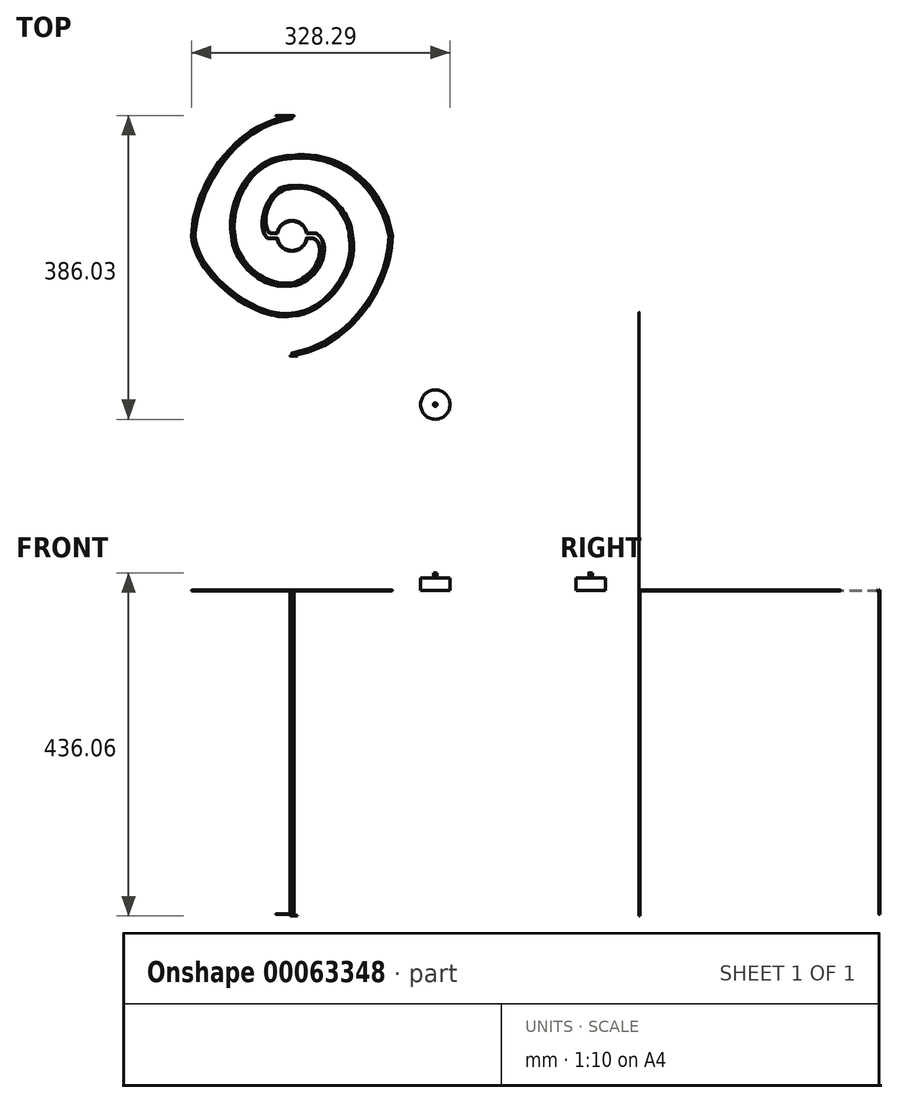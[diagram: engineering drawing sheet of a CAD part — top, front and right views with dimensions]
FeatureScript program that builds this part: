
annotation { "Feature Type Name" : "Feature", "Feature Type Description" : "" }
export const myFeature = defineFeature(function(context is Context, id is Id, definition is map)
    precondition{}
    {
        {
            var Q0;
            Q0=qCreatedBy(makeId("Top.planeOp"),FACE);
            var sketch = newSketch(context, id + "F0", { "sketchPlane" : qUnion([Q0])});
            skArc(sketch, "E0", {"start": v(0, 89.77) * mm, "mid": v(-59.8, 59.94) * mm, "end": v(-89.32, 0) * mm});
            skArc(sketch, "E1", {"start": v(-89.32, 0) * mm, "mid": v(-62.36, -58.9) * mm, "end": v(0, -76.43) * mm});
            skArc(sketch, "E2", {"start": v(0, -76.43) * mm, "mid": v(50.12, -52.11) * mm, "end": v(69.78, 0) * mm});
            skArc(sketch, "E3", {"start": v(69.78, 0) * mm, "mid": v(43.04, 36.2) * mm, "end": v(0, 49.33) * mm});
            skArc(sketch, "E4", {"start": v(0, 49.33) * mm, "mid": v(-33.38, 33.39) * mm, "end": v(-49.32, 0) * mm});
            skArc(sketch, "E5", {"start": v(-49.32, 0) * mm, "mid": v(-33.62, -32.42) * mm, "end": v(0, -45.36) * mm});
            skArc(sketch, "E6", {"start": v(0, -45.36) * mm, "mid": v(28.3, -30.82) * mm, "end": v(36.16, 0) * mm});
            skArc(sketch, "E7", {"start": v(36.16, 0) * mm, "mid": v(22.2, 17.77) * mm, "end": v(0, 22) * mm});
            skArc(sketch, "E8", {"start": v(0, 22) * mm, "mid": v(-15.87, 15.65) * mm, "end": v(-22.73, 0) * mm});
            skArc(sketch, "E9", {"start": v(-22.73, 0) * mm, "mid": v(-20.93, -10.33) * mm, "end": v(-11.38, -14.66) * mm});
            skLineSegment(sketch, "E10", {"start": v(-11.38, -14.66) * mm, "end": v(-4.56, -14.24) * mm});
            skArc(sketch, "E11", {"start": v(-4.56, -14.24) * mm, "mid": v(3.25, -18.93) * mm, "end": v(11.06, -14.24) * mm});
            skLineSegment(sketch, "E12", {"start": v(11.06, -14.24) * mm, "end": v(18.26, -14.24) * mm});
            skArc(sketch, "E13", {"start": v(0, -26.3) * mm, "mid": v(11.6, -24.01) * mm, "end": v(18.26, -14.24) * mm});
            skArc(sketch, "E14", {"start": v(-31.78, 0) * mm, "mid": v(-21.36, -19.76) * mm, "end": v(0, -26.3) * mm});
            skArc(sketch, "E15", {"start": v(0, 31.04) * mm, "mid": v(-22.27, 22.05) * mm, "end": v(-31.78, 0) * mm});
            skArc(sketch, "E16", {"start": v(45.44, 0) * mm, "mid": v(28.67, 24.24) * mm, "end": v(0, 31.04) * mm});
            skArc(sketch, "E17", {"start": v(0, -54.54) * mm, "mid": v(34.81, -37.34) * mm, "end": v(45.44, 0) * mm});
            skArc(sketch, "E18", {"start": v(-68.7, 0) * mm, "mid": v(-45.81, -41.72) * mm, "end": v(0, -54.54) * mm});
            skArc(sketch, "E19", {"start": v(0, 58.55) * mm, "mid": v(-46.84, 43.93) * mm, "end": v(-68.7, 0) * mm});
            skArc(sketch, "E20", {"start": v(83.03, 0) * mm, "mid": v(51.48, 43.4) * mm, "end": v(0, 58.55) * mm});
            skArc(sketch, "E21", {"start": v(0, -90.65) * mm, "mid": v(60.43, -62.65) * mm, "end": v(83.03, 0) * mm});
            skSolve(sketch);
        }
        {
            var Q0;
            Q0=qCreatedBy(makeId("Top.planeOp"),FACE);
            var sketch = newSketch(context, id + "F1", { "sketchPlane" : qUnion([Q0])});
            skCircle(sketch, "E22", {"center": v(353.44, -9.02) * mm, "radius": 19.05 * mm});
            skCircle(sketch, "E23", {"center": v(353.44, -9.02) * mm, "radius": 38.5 * mm});
            skCircle(sketch, "E24", {"center": v(353.44, -9.02) * mm, "radius": 41.67 * mm});
            skCircle(sketch, "E25", {"center": v(353.44, -9.02) * mm, "radius": 84.25 * mm});
            skCircle(sketch, "E26", {"center": v(353.44, -9.02) * mm, "radius": 87.43 * mm});
            skCircle(sketch, "E27", {"center": v(353.44, -9.02) * mm, "radius": 149.22 * mm});
            skCircle(sketch, "E28", {"center": v(353.44, -9.02) * mm, "radius": 152.4 * mm});
            skLineSegment(sketch, "E29", {"start": v(353.44, -9.02) * mm, "end": v(148.9, -9.02) * mm, "construction": true});
            skLineSegment(sketch, "E30", {"start": v(148.9, -9.02) * mm, "end": v(530.73, -9.02) * mm, "construction": true});
            skPoint(sketch, "E30.endSnap0", {"position": v(251.17, -9.02) * mm});
            skFitSpline(sketch, "E31", {"points": [v(353.44, 143.38) * mm, v(223.56, -9.02) * mm, v(353.44, -96.44) * mm], "startDerivative": vector(-431.97, -40.6) * mm, "endDerivative": vector(377.83, 174.24) * mm});
            skFitSpline(sketch, "E32", {"points": [v(353.44, -96.44) * mm, v(412.8, -9.02) * mm], "startDerivative": vector(88.92, 25.68) * mm, "endDerivative": vector(-23.7, 167.58) * mm});
            skFitSpline(sketch, "E33", {"points": [v(412.8, -9.02) * mm, v(353.44, 32.65) * mm], "startDerivative": vector(-4.13, 75.4) * mm, "endDerivative": vector(-93.38, -20.84) * mm});
            skFitSpline(sketch, "E34", {"points": [v(353.44, 32.65) * mm, v(319.45, -9.02) * mm], "startDerivative": vector(-79.71, -28.71) * mm, "endDerivative": vector(3.4, -46.05) * mm});
            skLineSegment(sketch, "E35", {"start": v(319.45, -9.02) * mm, "end": v(319.45, -13.48) * mm});
            skLineSegment(sketch, "E36", {"start": v(319.45, -13.48) * mm, "end": v(334.92, -13.48) * mm});
            skArc(sketch, "E37", {"start": v(334.92, -13.48) * mm, "mid": v(353.44, -28.18) * mm, "end": v(371.95, -13.48) * mm});
            skLineSegment(sketch, "E38", {"start": v(371.95, -13.48) * mm, "end": v(380.93, -13.48) * mm});
            skFitSpline(sketch, "E39", {"points": [v(380.93, -13.48) * mm, v(353.44, -47.5) * mm], "startDerivative": vector(2.43, -44.73) * mm, "endDerivative": vector(-36.66, -5.97) * mm});
            skFitSpline(sketch, "E40", {"points": [v(353.44, -47.5) * mm, v(291.41, -9.02) * mm], "startDerivative": vector(-111.15, -35.33) * mm, "endDerivative": vector(9.25, 49.7) * mm});
            skFitSpline(sketch, "E41", {"points": [v(291.41, -9.02) * mm, v(353.09, 75.24) * mm], "startDerivative": vector(8.63, 128.1) * mm, "endDerivative": vector(83.56, 34.12) * mm});
            skFitSpline(sketch, "E42", {"points": [v(353.09, 75.24) * mm, v(470.5, -9.02) * mm], "startDerivative": vector(188.1, 69.59) * mm, "endDerivative": vector(-1.84, -118.92) * mm});
            skFitSpline(sketch, "E43", {"points": [v(470.5, -9.02) * mm, v(353.44, -158.24) * mm], "startDerivative": vector(5.2, -214.31) * mm, "endDerivative": vector(-145.21, 3.55) * mm});
            skLineSegment(sketch, "E44", {"start": v(353.44, -9.02) * mm, "end": v(353.44, 175.95) * mm, "construction": true});
            skLineSegment(sketch, "E45", {"start": v(353.44, 175.95) * mm, "end": v(353.44, -184.71) * mm, "construction": true});
            skSolve(sketch);
        }
        {
            var Q0;
            {var subQ0=sQuery(id+"F1.wireOp",EDGE,"E31");var subQ3=sQuery(id+"F1.wireOp",EDGE,"E27");var subQ4=makeQuery(id+"F1.imprint","INTERSECT",VERTEX,{"derivedFrom":[subQ3,subQ0]});Q0=makeQuery(id+"F1.imprint","IMPRINT",FACE,{"disambiguationData":[TD([[makeQuery(id+"F1.imprint","IMPRINT",EDGE,{"disambiguationData":[TD([[subQ4,1.0]])],"derivedFrom":subQ3}),1.0]])]});}
            var sketch = newSketch(context, id + "F2", { "sketchPlane" : qUnion([Q0])});
            skLineSegment(sketch, "E46", {"start": v(223.56, -9.02) * mm, "end": v(226.73, -9.02) * mm, "construction": true});
            skFitSpline(sketch, "E47", {"points": [v(353.44, 140.05) * mm, v(226.73, -9.02) * mm], "startDerivative": vector(-240.84, -35.76) * mm, "endDerivative": vector(17.36, -172.87) * mm});
            skFitSpline(sketch, "E48", {"points": [v(226.73, -9.02) * mm, v(353.45, -93.24) * mm], "startDerivative": vector(25.64, -131.53) * mm, "endDerivative": vector(239.43, 63.9) * mm});
            skLineSegment(sketch, "E49", {"start": v(412.8, -9.02) * mm, "end": v(409.62, -9.02) * mm, "construction": true});
            skFitSpline(sketch, "E50", {"points": [v(353.45, -93.24) * mm, v(409.62, -9.02) * mm], "startDerivative": vector(110.05, 33.72) * mm, "endDerivative": vector(-18.44, 120.08) * mm});
            skFitSpline(sketch, "E51", {"points": [v(409.62, -9.02) * mm, v(353.4, 29.47) * mm], "startDerivative": vector(8.18, 31.72) * mm, "endDerivative": vector(-112.73, -30.61) * mm});
            skLineSegment(sketch, "E52", {"start": v(319.45, -9.02) * mm, "end": v(322.62, -9.02) * mm, "construction": true});
            skLineSegment(sketch, "E53", {"start": v(322.62, -9.02) * mm, "end": v(322.62, -4.55) * mm, "construction": true});
            skFitSpline(sketch, "E54", {"points": [v(353.4, 29.47) * mm, v(322.62, -4.55) * mm], "startDerivative": vector(-80.37, -22.35) * mm, "endDerivative": vector(1.16, -19.89) * mm});
            skLineSegment(sketch, "E55", {"start": v(329.9, -4.55) * mm, "end": v(334.83, -4.55) * mm});
            skArc(sketch, "E56", {"start": v(372.09, -4.55) * mm, "mid": v(353.46, 9.97) * mm, "end": v(334.83, -4.55) * mm});
            skLineSegment(sketch, "E57", {"start": v(372.09, -4.55) * mm, "end": v(379.21, -4.55) * mm});
            skFitSpline(sketch, "E58", {"points": [v(386.3, -4.55) * mm, v(353.39, -50.78) * mm], "startDerivative": vector(-6.93, -100.77) * mm, "endDerivative": vector(-36.58, -8.8) * mm});
            skLineSegment(sketch, "E59", {"start": v(291.41, -9.02) * mm, "end": v(288.24, -9.02) * mm, "construction": true});
            skFitSpline(sketch, "E60", {"points": [v(353.39, -50.78) * mm, v(288.24, -9.02) * mm], "startDerivative": vector(-119.3, -24.8) * mm, "endDerivative": vector(-0.62, 72.94) * mm});
            skFitSpline(sketch, "E61", {"points": [v(288.24, -9.02) * mm, v(353.34, 78.42) * mm], "startDerivative": vector(-1.96, 107.07) * mm, "endDerivative": vector(111.54, 29.74) * mm});
            skLineSegment(sketch, "E62", {"start": v(470.5, -9.02) * mm, "end": v(473.67, -9.02) * mm, "construction": true});
            skFitSpline(sketch, "E63", {"points": [v(353.34, 78.42) * mm, v(473.67, -9.02) * mm], "startDerivative": vector(122.78, 60.33) * mm, "endDerivative": vector(4.5, -189.18) * mm});
            skFitSpline(sketch, "E64", {"points": [v(473.67, -9.02) * mm, v(353.43, -161.4) * mm], "startDerivative": vector(21.27, -226.04) * mm, "endDerivative": vector(-143.25, 5.34) * mm});
            skArc(sketch, "E65.filletArc", {"start": v(385.49, -11.87) * mm, "mid": v(384.04, -6.76) * mm, "end": v(379.21, -4.55) * mm});
            skArc(sketch, "E66.filletArc", {"start": v(323.83, 3.67) * mm, "mid": v(324.8, -1.97) * mm, "end": v(329.9, -4.55) * mm});
            skSolve(sketch);
        }
        {
            var Q0;
            Q0=qCreatedBy(makeId("Right.planeOp"),FACE);
            var Q1;
            Q1=sQuery(id+"F1.wireOp",VERTEX,"E23.center");
            cPlane(context, id + "F3", {"entities" : qUnion([Q0, Q1]), "cplaneType" : CPlaneType.PLANE_POINT, "offset" : 152.4 * mm, "width" : 152.4 * mm, "height" : 152.4 * mm});
        }
        {
            var Q0;
            Q0=qCreatedBy(id+"F3.planeOp",FACE);
            var sketch = newSketch(context, id + "F4", { "sketchPlane" : qUnion([Q0])});
            skCircle(sketch, "E67", {"center": v(-161.4, 0) * mm, "radius": 0.53 * mm});
            skSolve(sketch);
        }
        {
            var Q0;
            Q0=qCreatedBy(makeId("Top.planeOp"),FACE);
            var sketch = newSketch(context, id + "F5", { "sketchPlane" : qUnion([Q0])});
            skCircle(sketch, "E68", {"center": v(-330.96, 0) * mm, "radius": 152.4 * mm, "construction": true});
            skLineSegment(sketch, "E69", {"start": v(-330.96, 0) * mm, "end": v(-330.96, 174.6) * mm, "construction": true});
            skLineSegment(sketch, "E70", {"start": v(-330.96, 174.6) * mm, "end": v(-330.96, -229.43) * mm, "construction": true});
            skLineSegment(sketch, "E71", {"start": v(-330.96, -229.43) * mm, "end": v(-330.96, 0) * mm, "construction": true});
            skLineSegment(sketch, "E72", {"start": v(-512.76, 0) * mm, "end": v(-151.64, 0) * mm, "construction": true});
            skLineSegment(sketch, "E73", {"start": v(-330.96, 0) * mm, "end": v(-330.96, 3.18) * mm, "construction": true});
            skLineSegment(sketch, "E74", {"start": v(-330.96, 0) * mm, "end": v(-330.96, -3.17) * mm, "construction": true});
            skArc(sketch, "E75", {"start": v(-312.18, 3.17) * mm, "mid": v(-330.96, 19.05) * mm, "end": v(-349.75, 3.17) * mm});
            skLineSegment(sketch, "E76", {"start": v(-349.75, 3.18) * mm, "end": v(-358.64, 3.18) * mm});
            skLineSegment(sketch, "E77", {"start": v(-349.75, -3.17) * mm, "end": v(-361.81, -3.17) * mm});
            skLineSegment(sketch, "E78", {"start": v(-312.18, 3.18) * mm, "end": v(-300.11, 3.18) * mm});
            skLineSegment(sketch, "E79", {"start": v(-312.18, -3.17) * mm, "end": v(-303.29, -3.17) * mm});
            skArc(sketch, "E80.trimOffspring", {"start": v(-349.75, -3.17) * mm, "mid": v(-330.96, -19.05) * mm, "end": v(-312.18, -3.17) * mm});
            skLineSegment(sketch, "E81", {"start": v(-178.56, 0) * mm, "end": v(-203.96, 0) * mm, "construction": true});
            skLineSegment(sketch, "E82", {"start": v(-330.96, 152.4) * mm, "end": v(-330.96, 101.6) * mm, "construction": true});
            skLineSegment(sketch, "E83", {"start": v(-483.36, 0) * mm, "end": v(-407.16, 0) * mm, "construction": true});
            skLineSegment(sketch, "E84", {"start": v(-330.96, -152.4) * mm, "end": v(-330.96, -63.5) * mm, "construction": true});
            skFitSpline(sketch, "E85", {"points": [v(-330.96, -152.4) * mm, v(-203.96, 0) * mm], "startDerivative": vector(230.37, 35.35) * mm, "endDerivative": vector(4.4, 184.96) * mm});
            skFitSpline(sketch, "E86", {"points": [v(-203.96, 0) * mm, v(-330.96, 101.6) * mm], "startDerivative": vector(-30.58, 196.85) * mm, "endDerivative": vector(-179.41, -25.24) * mm});
            skFitSpline(sketch, "E87", {"points": [v(-330.96, 101.6) * mm, v(-407.16, 0) * mm], "startDerivative": vector(-173.45, -0.7) * mm, "endDerivative": vector(21.4, -112.1) * mm});
            skFitSpline(sketch, "E88", {"points": [v(-407.16, 0) * mm, v(-330.96, -63.5) * mm], "startDerivative": vector(0.84, -99.87) * mm, "endDerivative": vector(111.18, 19.14) * mm});
            skFitSpline(sketch, "E89", {"points": [v(-330.96, -63.5) * mm, v(-300.11, 3.18) * mm], "startDerivative": vector(103.4, 14) * mm, "endDerivative": vector(-69.01, 47.05) * mm});
            skLineSegment(sketch, "E90", {"start": v(-483.36, 0) * mm, "end": v(-457.96, 0) * mm, "construction": true});
            skLineSegment(sketch, "E91", {"start": v(-330.96, -152.4) * mm, "end": v(-330.96, -101.6) * mm, "construction": true});
            skLineSegment(sketch, "E92", {"start": v(-178.56, 0) * mm, "end": v(-254.76, 0) * mm, "construction": true});
            skLineSegment(sketch, "E93", {"start": v(-330.96, 152.4) * mm, "end": v(-330.96, 63.5) * mm, "construction": true});
            skFitSpline(sketch, "E94", {"points": [v(-330.96, 152.4) * mm, v(-457.96, 0) * mm], "startDerivative": vector(-240.8, -34.76) * mm, "endDerivative": vector(-3.06, -164.07) * mm});
            skFitSpline(sketch, "E95", {"points": [v(-457.96, 0) * mm, v(-330.96, -101.6) * mm], "startDerivative": vector(11.63, -156.74) * mm, "endDerivative": vector(133.05, 24.6) * mm});
            skFitSpline(sketch, "E96", {"points": [v(-330.96, -101.6) * mm, v(-254.76, 0) * mm], "startDerivative": vector(127.5, 6.41) * mm, "endDerivative": vector(-31.42, 132.25) * mm});
            skFitSpline(sketch, "E97", {"points": [v(-254.76, 0) * mm, v(-330.96, 63.5) * mm], "startDerivative": vector(0.8, 91.83) * mm, "endDerivative": vector(-115.53, -17.65) * mm});
            skFitSpline(sketch, "E98", {"points": [v(-330.96, 63.5) * mm, v(-361.81, -3.18) * mm], "startDerivative": vector(-90.19, 5.4) * mm, "endDerivative": vector(51.52, -47.47) * mm});
            skLineSegment(sketch, "E99", {"start": v(-330.96, 152.4) * mm, "end": v(-330.96, 149.22) * mm, "construction": true});
            skLineSegment(sketch, "E100", {"start": v(-457.96, 0) * mm, "end": v(-454.79, 0) * mm, "construction": true});
            skLineSegment(sketch, "E101", {"start": v(-330.96, -101.6) * mm, "end": v(-330.96, -98.42) * mm, "construction": true});
            skLineSegment(sketch, "E102", {"start": v(-254.76, 0) * mm, "end": v(-257.94, 0) * mm, "construction": true});
            skLineSegment(sketch, "E103", {"start": v(-330.96, 63.5) * mm, "end": v(-330.96, 60.33) * mm, "construction": true});
            skFitSpline(sketch, "E104", {"points": [v(-358.64, 3.17) * mm, v(-330.96, 60.33) * mm], "startDerivative": vector(-42.74, 33.07) * mm, "endDerivative": vector(87.53, -3.24) * mm});
            skFitSpline(sketch, "E105", {"points": [v(-330.96, 60.33) * mm, v(-257.94, 0) * mm], "startDerivative": vector(114.15, 19.98) * mm, "endDerivative": vector(3.36, -90.65) * mm});
            skFitSpline(sketch, "E106", {"points": [v(-257.94, 0) * mm, v(-330.96, -98.42) * mm], "startDerivative": vector(30.25, -130.25) * mm, "endDerivative": vector(-123.7, -5.42) * mm});
            skFitSpline(sketch, "E107", {"points": [v(-330.96, -98.42) * mm, v(-454.79, 0) * mm], "startDerivative": vector(-132.94, -24.8) * mm, "endDerivative": vector(-14.32, 147.87) * mm});
            skFitSpline(sketch, "E108", {"points": [v(-454.79, 0) * mm, v(-330.96, 149.22) * mm], "startDerivative": vector(10.78, 162.43) * mm, "endDerivative": vector(236.5, 36.1) * mm});
            skLineSegment(sketch, "E109", {"start": v(-330.96, -152.4) * mm, "end": v(-330.96, -149.22) * mm, "construction": true});
            skLineSegment(sketch, "E110", {"start": v(-203.96, 0) * mm, "end": v(-207.14, 0) * mm, "construction": true});
            skLineSegment(sketch, "E111", {"start": v(-330.96, 101.6) * mm, "end": v(-330.96, 98.42) * mm, "construction": true});
            skLineSegment(sketch, "E112", {"start": v(-407.16, 0) * mm, "end": v(-403.99, 0) * mm, "construction": true});
            skLineSegment(sketch, "E113", {"start": v(-330.96, -63.5) * mm, "end": v(-330.96, -60.33) * mm, "construction": true});
            skFitSpline(sketch, "E114", {"points": [v(-303.29, -3.17) * mm, v(-330.96, -60.33) * mm], "startDerivative": vector(57.31, -36.87) * mm, "endDerivative": vector(-88.58, -20.87) * mm});
            skFitSpline(sketch, "E115", {"points": [v(-330.96, -60.33) * mm, v(-403.99, 0) * mm], "startDerivative": vector(-109.68, -14.12) * mm, "endDerivative": vector(-5.89, 94.5) * mm});
            skFitSpline(sketch, "E116", {"points": [v(-403.99, 0) * mm, v(-330.96, 98.42) * mm], "startDerivative": vector(-18.97, 110.61) * mm, "endDerivative": vector(163.74, 1.65) * mm});
            skFitSpline(sketch, "E117", {"points": [v(-330.96, 98.42) * mm, v(-207.14, 0) * mm], "startDerivative": vector(172, 23.11) * mm, "endDerivative": vector(33.66, -186.98) * mm});
            skFitSpline(sketch, "E118", {"points": [v(-207.14, 0) * mm, v(-330.96, -149.22) * mm], "startDerivative": vector(-3.34, -180.33) * mm, "endDerivative": vector(-222.34, -34.87) * mm});
            skSolve(sketch);
        }
        {
            var Q0;
            Q0=qCreatedBy(makeId("Right.planeOp"),FACE);
            var Q1;
            Q1=sQuery(id+"F5.wireOp",VERTEX,"E71.end");
            cPlane(context, id + "F6", {"entities" : qUnion([Q0, Q1]), "cplaneType" : CPlaneType.PLANE_POINT, "offset" : 152.4 * mm, "width" : 152.4 * mm, "height" : 152.4 * mm});
        }
        {
            var Q0;
            Q0=qCreatedBy(id+"F6.planeOp",FACE);
            var sketch = newSketch(context, id + "F7", { "sketchPlane" : qUnion([Q0])});
            skCircle(sketch, "E119", {"center": v(-152.4, 0) * mm, "radius": 0.53 * mm});
            skSolve(sketch);
        }
        {
            var Q0;
            Q0=qCreatedBy(id+"F6.planeOp",FACE);
            var sketch = newSketch(context, id + "F8", { "sketchPlane" : qUnion([Q0])});
            skCircle(sketch, "E120", {"center": v(152.4, 0) * mm, "radius": 0.53 * mm});
            skSolve(sketch);
        }
        {
            var Q0;
            Q0 = qSketchRegion(id + "F7", true);
            var Q1;
            Q1=sQuery(id+"F5.wireOp",EDGE,"E85");
            var Q2;
            Q2=sQuery(id+"F5.wireOp",EDGE,"E86");
            var Q3;
            Q3=sQuery(id+"F5.wireOp",EDGE,"E87");
            var Q4;
            Q4=sQuery(id+"F5.wireOp",EDGE,"E88");
            var Q5;
            Q5=sQuery(id+"F5.wireOp",EDGE,"E89");
            var Q6;
            Q6=sQuery(id+"F5.wireOp",EDGE,"E78");
            var Q7;
            Q7=sQuery(id+"F5.wireOp",EDGE,"E75");
            var Q8;
            Q8=sQuery(id+"F5.wireOp",EDGE,"E76");
            var Q9;
            Q9=sQuery(id+"F5.wireOp",EDGE,"E104");
            var Q10;
            Q10=sQuery(id+"F5.wireOp",EDGE,"E105");
            var Q11;
            Q11=sQuery(id+"F5.wireOp",EDGE,"E106");
            var Q12;
            Q12=sQuery(id+"F5.wireOp",EDGE,"E107");
            var Q13;
            Q13=sQuery(id+"F5.wireOp",EDGE,"E108");
            sweep(context, id + "F9", {"profiles" : qUnion([Q0]), "path" : qUnion([Q1, Q2, Q3, Q4, Q5, Q6, Q7, Q8, Q9, Q10, Q11, Q12, Q13])});
        }
        {
            var Q0;
            Q0 = qSketchRegion(id + "F8", true);
            var Q1;
            Q1=sQuery(id+"F5.wireOp",EDGE,"E94");
            var Q2;
            Q2=sQuery(id+"F5.wireOp",EDGE,"E95");
            var Q3;
            Q3=sQuery(id+"F5.wireOp",EDGE,"E96");
            var Q4;
            Q4=sQuery(id+"F5.wireOp",EDGE,"E97");
            var Q5;
            Q5=sQuery(id+"F5.wireOp",EDGE,"E98");
            var Q6;
            Q6=sQuery(id+"F5.wireOp",EDGE,"E77");
            var Q7;
            Q7=sQuery(id+"F5.wireOp",EDGE,"E80.trimOffspring");
            var Q8;
            Q8=sQuery(id+"F5.wireOp",EDGE,"E79");
            var Q9;
            Q9=sQuery(id+"F5.wireOp",EDGE,"E114");
            var Q10;
            Q10=sQuery(id+"F5.wireOp",EDGE,"E115");
            var Q11;
            Q11=sQuery(id+"F5.wireOp",EDGE,"E116");
            var Q12;
            Q12=sQuery(id+"F5.wireOp",EDGE,"E117");
            var Q13;
            Q13=sQuery(id+"F5.wireOp",EDGE,"E118");
            sweep(context, id + "F10", {"profiles" : qUnion([Q0]), "path" : qUnion([Q1, Q2, Q3, Q4, Q5, Q6, Q7, Q8, Q9, Q10, Q11, Q12, Q13])});
        }
        {
            var Q0;
            Q0=qCreatedBy(makeId("Top.planeOp"),FACE);
            var sketch = newSketch(context, id + "F11", { "sketchPlane" : qUnion([Q0])});
            skCircle(sketch, "E121", {"center": v(-148.86, -214.43) * mm, "radius": 18.67 * mm});
            skSolve(sketch);
        }
        {
            var Q0;
            Q0=makeQuery(id+"F11.imprint","IMPRINT",FACE,{"disambiguationData":[TD([[makeQuery(id+"F11.imprint","IMPRINT",EDGE,{"derivedFrom":sQuery(id+"F11.wireOp",EDGE,"E121")}),1.0]])]});
            extrude(context, id + "F12", {"entities" : qUnion([Q0]), "depth" : 15.6 * mm});
        }
        {
            var Q0;
            Q0=makeQuery(id+"F12.opExtrude","CAP_FACE",FACE,{"disambiguationData":[OSD([sQuery(id+"F11.wireOp",EDGE,"E121")])],"isStart":false});
            var sketch = newSketch(context, id + "F13", { "sketchPlane" : qUnion([Q0])});
            skCircle(sketch, "E122", {"center": v(-148.86, -214.43) * mm, "radius": 2.24 * mm});
            skSolve(sketch);
        }
        {
            var Q0;
            Q0 = qSketchRegion(id + "F13", true);
            extrude(context, id + "F14", {"entities" : qUnion([Q0]), "operationType" : NewBodyOperationType.ADD, "depth" : 6.7 * mm});
        }
        {
            var Q0;
            Q0=qCreatedBy(makeId("Front.planeOp"),FACE);
            var Q1;
            Q1=sQuery(id+"F7.wireOp",VERTEX,"E119.center");
            cPlane(context, id + "F15", {"entities" : qUnion([Q0, Q1]), "cplaneType" : CPlaneType.PLANE_POINT, "offset" : 152.4 * mm, "width" : 152.4 * mm, "height" : 152.4 * mm});
        }
        {
            var Q0;
            Q0=qCreatedBy(id+"F15.planeOp",FACE);
            var sketch = newSketch(context, id + "F16", { "sketchPlane" : qUnion([Q0])});
            skLineSegment(sketch, "E123", {"start": v(-330.97, 0) * mm, "end": v(-331.63, 0) * mm});
            skLineSegment(sketch, "E124", {"start": v(-332.9, -1.27) * mm, "end": v(-332.9, -411.28) * mm});
            skPoint(sketch, "E125.visualSharp", {"position": v(-332.9, 0) * mm});
            skArc(sketch, "E125.filletArc", {"start": v(-331.63, 0) * mm, "mid": v(-332.53, -0.37) * mm, "end": v(-332.9, -1.27) * mm});
            skSolve(sketch);
        }
        {
            var Q0;
            Q0=makeQuery(id+"F9.opSweep","CAP_FACE",FACE,{"disambiguationData":[OSD([sQuery(id+"F5.wireOp",VERTEX,"E85.start"),sQuery(id+"F7.wireOp",EDGE,"E119")])],"isStart":true});
            var Q1;
            Q1=sQuery(id+"F16.wireOp",EDGE,"E123");
            var Q2;
            Q2=sQuery(id+"F16.wireOp",EDGE,"E125.filletArc");
            var Q3;
            Q3=sQuery(id+"F16.wireOp",EDGE,"E124");
            sweep(context, id + "F17", {"operationType" : NewBodyOperationType.ADD, "profiles" : qUnion([Q0]), "path" : qUnion([Q1, Q2, Q3])});
        }
        {
            var Q0;
            Q0=qCreatedBy(id+"F15.planeOp",FACE);
            var sketch = newSketch(context, id + "F18", { "sketchPlane" : qUnion([Q0])});
            skLineSegment(sketch, "E126", {"start": v(-332.87, -411.25) * mm, "end": v(-332.87, -411.92) * mm});
            skLineSegment(sketch, "E127", {"start": v(-331.6, -413.2) * mm, "end": v(-323.67, -413.2) * mm});
            skPoint(sketch, "E128.visualSharp", {"position": v(-332.87, -413.2) * mm});
            skArc(sketch, "E128.filletArc", {"start": v(-332.87, -411.92) * mm, "mid": v(-332.5, -412.82) * mm, "end": v(-331.6, -413.2) * mm});
            skSolve(sketch);
        }
        {
            var Q0;
            Q0=makeQuery(id+"F17.opSweep","CAP_FACE",FACE,{"disambiguationData":[OSD([sQuery(id+"F5.wireOp",VERTEX,"E85.start"),sQuery(id+"F7.wireOp",EDGE,"E119"),sQuery(id+"F16.wireOp",VERTEX,"E124.end")])],"isStart":false});
            var Q1;
            Q1=sQuery(id+"F18.wireOp",EDGE,"E126");
            var Q2;
            Q2=sQuery(id+"F18.wireOp",EDGE,"E128.filletArc");
            var Q3;
            Q3=sQuery(id+"F18.wireOp",EDGE,"E127");
            sweep(context, id + "F19", {"operationType" : NewBodyOperationType.ADD, "profiles" : qUnion([Q0]), "path" : qUnion([Q1, Q2, Q3])});
        }
        {
            var Q0;
            Q0=qCreatedBy(id+"F15.planeOp",FACE);
            var Q1;
            Q1=sQuery(id+"F8.wireOp",VERTEX,"E120.center");
            cPlane(context, id + "F20", {"entities" : qUnion([Q0, Q1]), "cplaneType" : CPlaneType.PLANE_POINT, "offset" : 152.4 * mm, "width" : 152.4 * mm, "height" : 152.4 * mm});
        }
        {
            var Q0;
            Q0=qCreatedBy(id+"F20.planeOp",FACE);
            var sketch = newSketch(context, id + "F21", { "sketchPlane" : qUnion([Q0])});
            skLineSegment(sketch, "E129", {"start": v(-330.96, 0) * mm, "end": v(-329.97, 0) * mm});
            skLineSegment(sketch, "E130", {"start": v(-328.7, -1.27) * mm, "end": v(-328.7, -410) * mm});
            skPoint(sketch, "E131.visualSharp", {"position": v(-328.7, 0) * mm});
            skArc(sketch, "E131.filletArc", {"start": v(-328.7, -1.27) * mm, "mid": v(-329.08, -0.37) * mm, "end": v(-329.97, 0) * mm});
            skLineSegment(sketch, "E132", {"start": v(-329.97, -411.28) * mm, "end": v(-351.8, -411.28) * mm});
            skPoint(sketch, "E133.visualSharp", {"position": v(-328.7, -411.28) * mm});
            skArc(sketch, "E133.filletArc", {"start": v(-329.97, -411.28) * mm, "mid": v(-329.08, -410.9) * mm, "end": v(-328.7, -410) * mm});
            skSolve(sketch);
        }
        {
            var Q0;
            Q0=makeQuery(id+"F8.imprint","IMPRINT",FACE,{"disambiguationData":[TD([[makeQuery(id+"F8.imprint","IMPRINT",EDGE,{"derivedFrom":sQuery(id+"F8.wireOp",EDGE,"E120")}),1.0]])]});
            var Q1;
            Q1=sQuery(id+"F21.wireOp",EDGE,"E129");
            var Q2;
            Q2=sQuery(id+"F21.wireOp",EDGE,"E131.filletArc");
            var Q3;
            Q3=sQuery(id+"F21.wireOp",EDGE,"E130");
            var Q4;
            Q4=sQuery(id+"F21.wireOp",EDGE,"E133.filletArc");
            var Q5;
            Q5=sQuery(id+"F21.wireOp",EDGE,"E132");
            sweep(context, id + "F22", {"operationType" : NewBodyOperationType.ADD, "profiles" : qUnion([Q0]), "path" : qUnion([Q1, Q2, Q3, Q4, Q5])});
        }
    });
